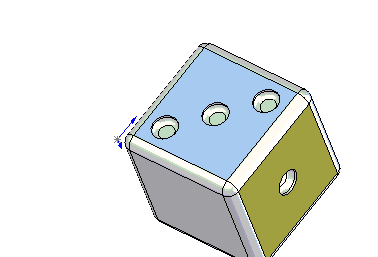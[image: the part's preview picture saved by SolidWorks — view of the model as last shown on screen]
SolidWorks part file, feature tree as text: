
SOLIDWORKS PART (.sldprt)
format: sldprt  version: not decoded by parser v0  size: 257,536 bytes
history: native  units: mm
features: sketch x5, fillet x5, cut_extrude x4, plane x3, extrude x1 + 1 further entry (+7 scaffold rows collapsed)
feature tree (26):
  scaffold x7  (default folders/planes/origin — collapsed)
  "Corps de surface"
  plane  "Face"
  plane  "Dessus"
  plane  "Droite"
  sketch  "Esquisse1"  dims[D1=50.0mm D2=50.0mm]
  extrude  "Extrusion1"  Depth=50mm
  sketch  "Esquisse2"  dims[D3=10.0mm D1=25.0mm D2=25.0mm]
  cut_extrude  "Enlèv. mat.-Extru.1"  Depth=3mm
  fillet  "Congé1"  Radius=2mm
  sketch  "Esquisse3"  dims[c1.D5=10.0mm c1.D6=10.0mm c2.D5=10.0mm c2.D7=~5.323049mm c2.D1=12.0mm c2.D2=12.0mm c2.D3=12.0mm c2.D4=12.0mm c3.D3=12.0mm c3.D4=12.0mm]
  cut_extrude  "Enlèv. mat.-Extru.3"  Depth=3mm
  fillet  "Congé3"  Radius=2mm
  sketch  "Esquisse4"  dims[c1.D1=~4.950621mm c1.D3=~2.210379mm c1.D5=~5.791576mm c2.D1=12.0mm c2.D2=12.0mm c2.D3=12.0mm c2.D4=12.0mm c2.D5=25.0mm c2.D6=25.0mm]
  cut_extrude  "Enlèv. mat.-Extru.4"  Depth=3mm
  fillet  "Congé4"  Radius=2mm
  sketch  "Esquisse5"  dims[c1.D1=~6.249504mm c1.D7=~6.263484mm c2.D1=12.0mm c2.D2=12.0mm c3.D1=12.0mm c3.D3=12.0mm c3.D4=12.0mm c3.D5=25.0mm c3.D6=25.0mm]
  cut_extrude  "Enlèv. mat.-Extru.5"  Depth=3mm
  fillet  "Congé5"  Radius=2mm
  fillet  "Congé6"  Radius=4mm
decode coverage: 15 of 15 modeling features carry decoded parameters; 1 rows unclassified (native names shown)
note: ~ marks probable driven/reference dimensions
note: suppression state not decoded; provenance and decode notes live in map.json
